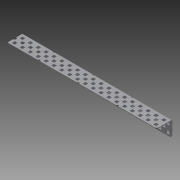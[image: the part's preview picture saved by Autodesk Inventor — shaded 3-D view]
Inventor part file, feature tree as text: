
AUTODESK INVENTOR PART (.ipt)
format: ipt  version: 2014 SP1 (Build 180222100, 222)  size: 1,577,472 bytes
history: native  units: in
note: dims shown in document units (in); Inventor stores cm internally (conversion verified against a paired STEP export)
features: other x1, imported_body x1, extrude x1, sketch x1
ambient origin geometry x8: Origin, YZ Plane, XZ Plane, XY Plane, X Axis, Y Axis, Z Axis, Center Point
bodies: Body1 (feature_tree)
feature tree (4):
  parser-record x1  (decoder bookkeeping rows leaked as tree rows — omitted from the tree; the rows remain in map.json)
  imported_body  "Base1"
  extrude  "Extrusion1"  Depth=1.0in TaperAngle=0.0deg
  sketch  "Sketch1"  dims[d0=3.0in d1=1.0in d2=0.0in]
